# Revit family: КМ Профиль_Универсальная потолочная стойка усиленная UPTU
name_source: partatom
category: Обобщенные модели
revit_build: Autodesk Revit 2016 (Build: 20160126_1600(x64)
units: mm (PartAtom-declared; Revit-internal decimal feet)

## family parameters
Всегда вертикально = Нет
Может служить основой для арматурных стержней = Нет
На основе рабочей плоскости = Нет
Общий = Нет
При загрузке вырезать с полостями = Нет
Размер круглого соединителя = Использовать диаметр
Тип детали = Нормальный
Точка расчета площади = Нет

## types (1)
- UPTU250
    Мсв.с = 4
    Мтрл.МатериалКрепленияКабельногоЛотка = <По категории>
    Рзм.B = 38 мм
    Рзм.L = 250 мм
    Рзм.d1 = 11 мм
    Рзм.d2 = 8 мм
    Рзм.dh1 = 10 мм
    Рзм.dl1 = 17 мм
    Рзм.l1 = 120 мм
    Рзм.l2 = 29 мм
    Рзм.s1 = 90 мм
    Рзм.s2 = 30 мм
    Рзм.t1 = 4 мм
    Рзм.t2 = 2.5 мм
    Спец.ЕдИзмКрепленияЛоткаКабельногоКанала = шт.
    Спец.ИзготовительКрепленияЛоткаКабельногоКанала = КМ Профиль
    Спец.КодОборудИзделияМатериалаКрепленияЛоткаКабельногоКанала = UPTU250
    Спец.МассаКрепленияЛоткаКабельногоКанала = 0.57 кг
    Спец.МассаТекстКрепленияЛоткаКабельногоКанала = 0.83
    Спец.НаименованиеИТенхХарКрепленияЛоткаКабельногоКанала = Универсальная потолочная стойка усиленная

## geometry (parser evidence)
native form markers: Blend x2
no freeform markers — native parametric forms only
